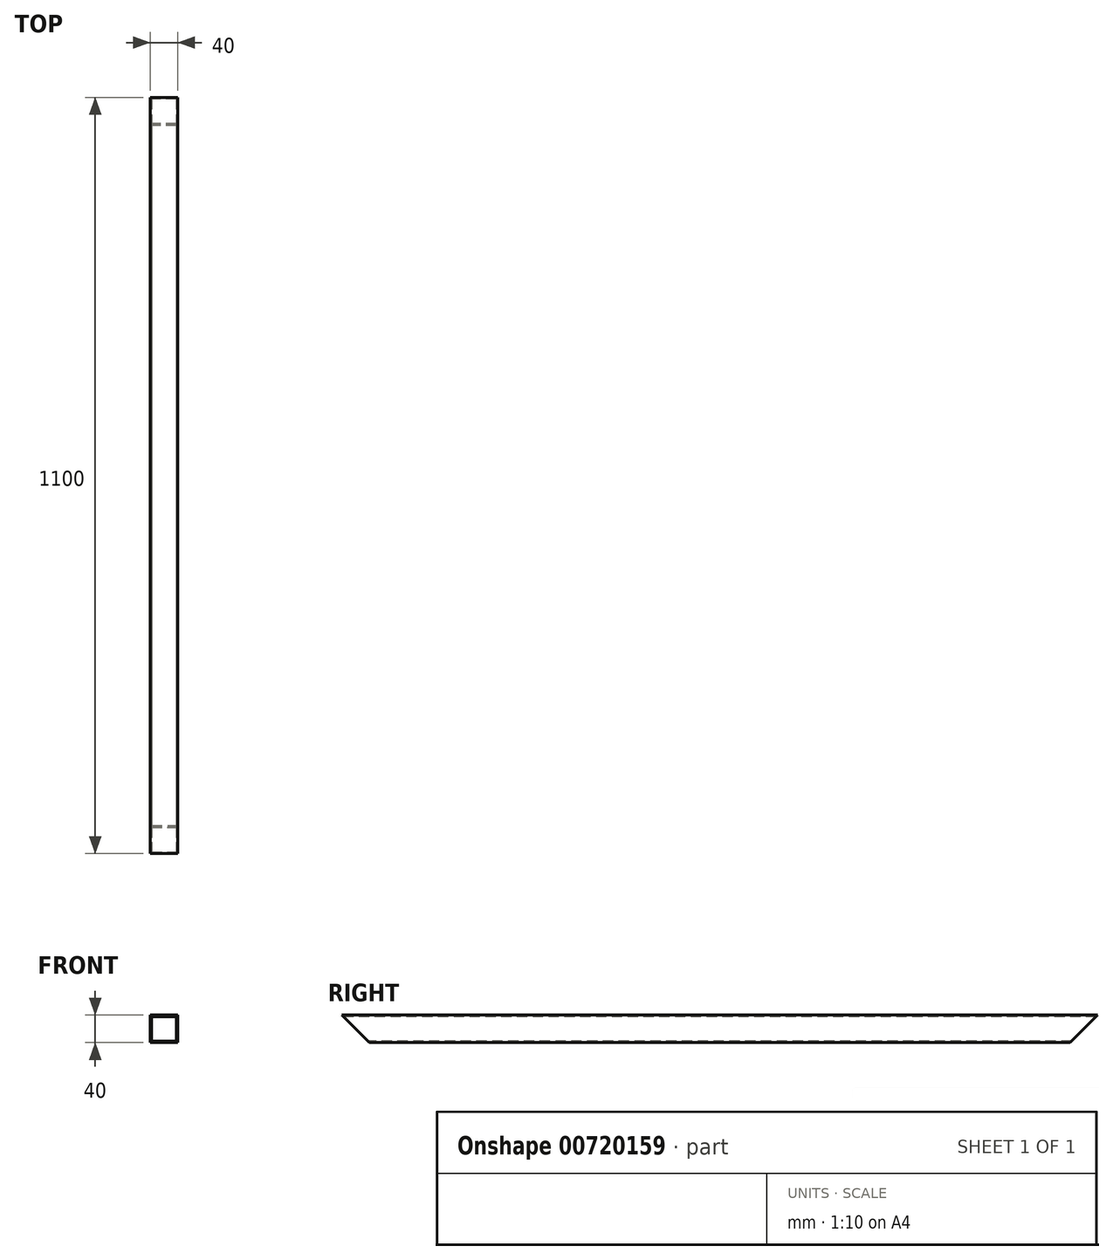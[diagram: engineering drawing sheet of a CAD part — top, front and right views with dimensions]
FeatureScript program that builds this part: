
annotation { "Feature Type Name" : "Feature", "Feature Type Description" : "" }
export const myFeature = defineFeature(function(context is Context, id is Id, definition is map)
    precondition{}
    {
        {
            var Q0;
            Q0=qCreatedBy(makeId("Front.planeOp"),FACE);
            var sketch = newSketch(context, id + "F0", { "sketchPlane" : qUnion([Q0])});
            skLineSegment(sketch, "E0.bottom", {"start": v(0, 0) * mm, "end": v(40, 0) * mm});
            skLineSegment(sketch, "E0.top", {"start": v(0, 40) * mm, "end": v(40, 40) * mm});
            skLineSegment(sketch, "E0.left", {"start": v(0, 0) * mm, "end": v(0, 40) * mm});
            skLineSegment(sketch, "E0.right", {"start": v(40, 0) * mm, "end": v(40, 40) * mm});
            skSolve(sketch);
        }
        {
            var Q0;
            Q0=qSketchRegion(id+"F0",true);
            extrude(context, id + "F1", {"entities" : qUnion([Q0]), "depth" : 1100 * mm, "offsetDistance" : 25 * mm});
        }
        {
            var Q0;
            Q0=makeQuery(id+"F1.opExtrude","CAP_FACE",FACE,{"disambiguationData":[OSD([sQuery(id+"F0.wireOp",EDGE,"E0.bottom"),sQuery(id+"F0.wireOp",EDGE,"E0.top"),sQuery(id+"F0.wireOp",EDGE,"E0.left"),sQuery(id+"F0.wireOp",EDGE,"E0.right")])],"isStart":false});
            var sketch = newSketch(context, id + "F2", { "sketchPlane" : qUnion([Q0])});
            skLineSegment(sketch, "E1.bottom", {"start": v(2, 2) * mm, "end": v(38, 2) * mm});
            skLineSegment(sketch, "E1.top", {"start": v(2, 38) * mm, "end": v(38, 38) * mm});
            skLineSegment(sketch, "E1.left", {"start": v(2, 2) * mm, "end": v(2, 38) * mm});
            skLineSegment(sketch, "E1.right", {"start": v(38, 2) * mm, "end": v(38, 38) * mm});
            skSolve(sketch);
        }
        {
            var Q0;
            Q0=makeQuery(id+"F2.imprint","IMPRINT",FACE,{"disambiguationData":[TD([[makeQuery(id+"F2.imprint","IMPRINT",EDGE,{"derivedFrom":sQuery(id+"F2.wireOp",EDGE,"E1.bottom")}),1.0]])]});
            extrude(context, id + "F3", {"entities" : qUnion([Q0]), "operationType" : NewBodyOperationType.REMOVE, "endBound" : BoundingType.THROUGH_ALL, "oppositeDirection" : true, "depth" : 25 * mm, "offsetDistance" : 25 * mm});
        }
        {
            var Q0;
            Q0=makeQuery(id+"F1.opExtrude","CAP_EDGE",EDGE,{"disambiguationData":[OSD([sQuery(id+"F0.wireOp",EDGE,"E0.bottom")])],"isStart":false});
            var Q1;
            Q1=makeQuery(id+"F1.opExtrude","CAP_EDGE",EDGE,{"disambiguationData":[OSD([sQuery(id+"F0.wireOp",EDGE,"E0.bottom")])],"isStart":true});
            chamfer(context, id + "F4", {"entities" : qUnion([Q0, Q1]), "width" : 40 * mm, "tangentPropagation" : true});
        }
    });
